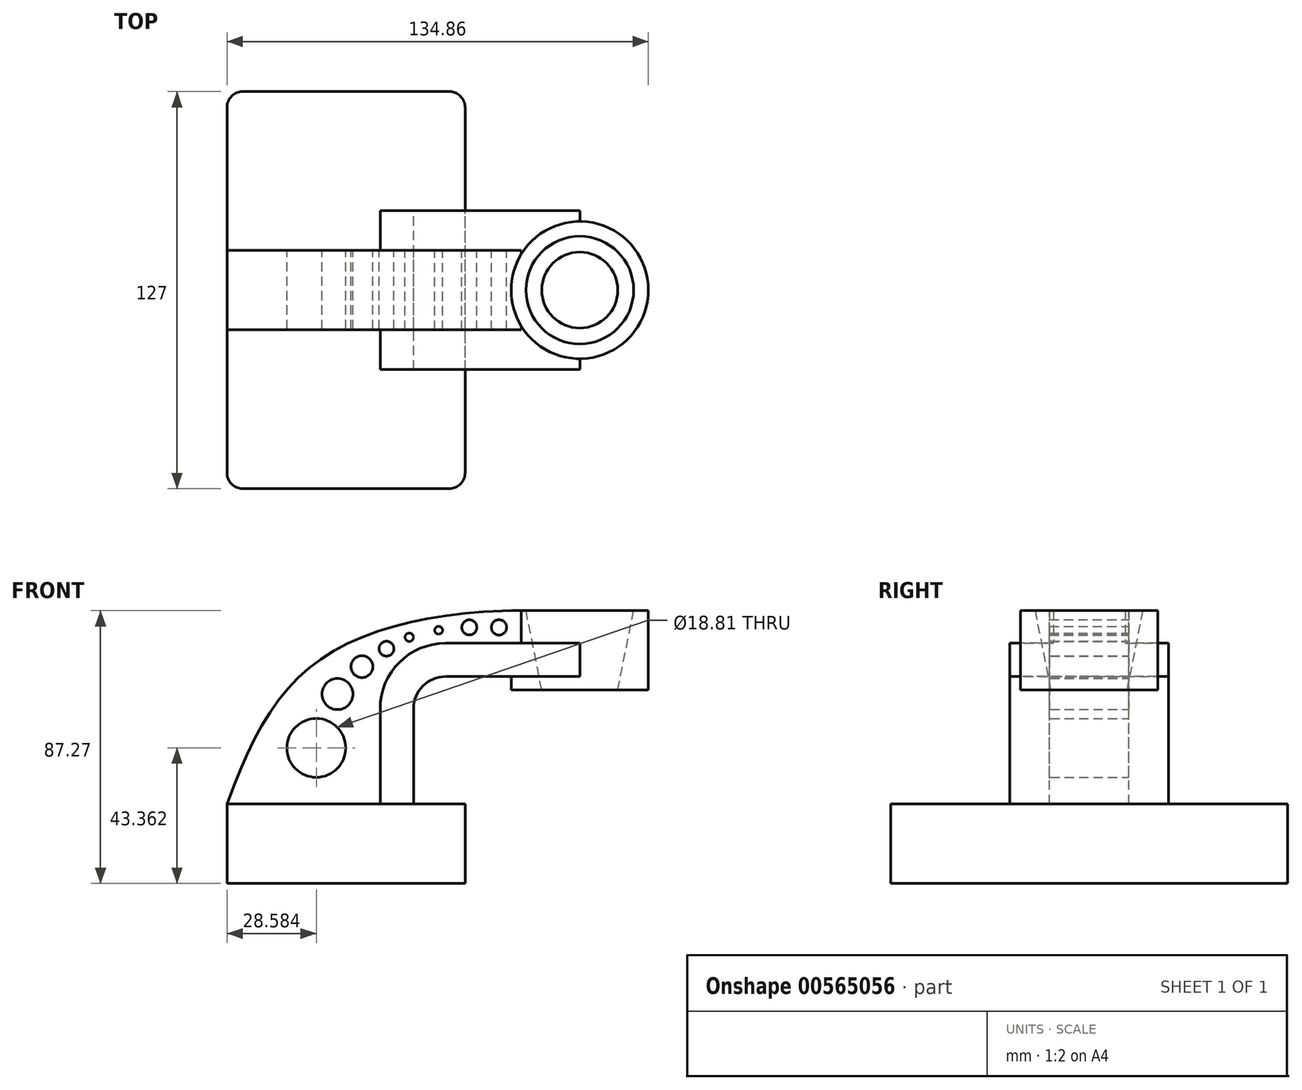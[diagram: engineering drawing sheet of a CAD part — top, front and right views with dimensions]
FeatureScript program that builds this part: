
annotation { "Feature Type Name" : "Feature", "Feature Type Description" : "" }
export const myFeature = defineFeature(function(context is Context, id is Id, definition is map)
    precondition{}
    {
        {
            var Q0;
            Q0=qCreatedBy(makeId("Front.planeOp"),FACE);
            var sketch = newSketch(context, id + "F0", { "sketchPlane" : qUnion([Q0])});
            skLineSegment(sketch, "E0.bottom", {"start": v(38.1, 12.7) * mm, "end": v(-38.1, 12.7) * mm});
            skLineSegment(sketch, "E0.top", {"start": v(38.1, -12.7) * mm, "end": v(-38.1, -12.7) * mm});
            skLineSegment(sketch, "E0.left", {"start": v(38.1, 12.7) * mm, "end": v(38.1, -12.7) * mm});
            skLineSegment(sketch, "E0.right", {"start": v(-38.1, 12.7) * mm, "end": v(-38.1, -12.7) * mm});
            skPoint(sketch, "E0.middle", {"position": v(0, 0) * mm});
            skLineSegment(sketch, "E1.bottom", {"start": v(96.76, 74.57) * mm, "end": v(56.12, 74.57) * mm});
            skLineSegment(sketch, "E1.top", {"start": v(96.76, 49.17) * mm, "end": v(56.12, 49.17) * mm});
            skLineSegment(sketch, "E1.left", {"start": v(96.76, 74.57) * mm, "end": v(96.76, 49.17) * mm});
            skLineSegment(sketch, "E1.right", {"start": v(56.12, 74.57) * mm, "end": v(56.12, 49.17) * mm});
            skPoint(sketch, "E1.middle", {"position": v(76.44, 61.87) * mm});
            skLineSegment(sketch, "E2", {"start": v(21.59, 12.7) * mm, "end": v(21.59, 43.18) * mm});
            skArc(sketch, "E3", {"start": v(31.88, 53.48) * mm, "mid": v(24.6, 50.46) * mm, "end": v(21.59, 43.18) * mm});
            skLineSegment(sketch, "E4", {"start": v(31.88, 53.48) * mm, "end": v(74.8, 53.48) * mm});
            skLineSegment(sketch, "E5.0", {"start": v(31.88, 64.15) * mm, "end": v(74.8, 64.15) * mm});
            skArc(sketch, "E5.1", {"start": v(31.88, 64.15) * mm, "mid": v(17.06, 58) * mm, "end": v(10.92, 43.18) * mm});
            skLineSegment(sketch, "E5.2", {"start": v(10.92, 12.7) * mm, "end": v(10.92, 43.18) * mm});
            skLineSegment(sketch, "E6", {"start": v(74.8, 49.17) * mm, "end": v(74.8, 74.57) * mm});
            skFitSpline(sketch, "E7", {"points": [v(-38.1, 12.7) * mm, v(-8.19, 58.97) * mm, v(56.12, 74.57) * mm], "startDerivative": vector(48.03, 130.43) * mm, "endDerivative": vector(140.44, 0) * mm});
            skLineSegment(sketch, "E8", {"start": v(86.96, 74.57) * mm, "end": v(86.96, 49.17) * mm});
            skLineSegment(sketch, "E9", {"start": v(86.96, 49.17) * mm, "end": v(92.04, 74.57) * mm});
            skLineSegment(sketch, "E10", {"start": v(92.04, 74.57) * mm, "end": v(86.96, 74.57) * mm});
            skCircle(sketch, "E11", {"center": v(-9.52, 30.66) * mm, "radius": 9.4 * mm});
            skCircle(sketch, "E12", {"center": v(-2.74, 47.88) * mm, "radius": 4.96 * mm});
            skCircle(sketch, "E13", {"center": v(5.1, 56.65) * mm, "radius": 3.49 * mm});
            skCircle(sketch, "E14", {"center": v(12.95, 62.4) * mm, "radius": 2.38 * mm});
            skCircle(sketch, "E15", {"center": v(20.24, 66.05) * mm, "radius": 1.35 * mm});
            skCircle(sketch, "E16", {"center": v(29.63, 68.3) * mm, "radius": 1.27 * mm});
            skCircle(sketch, "E17", {"center": v(39.47, 69.2) * mm, "radius": 2.42 * mm});
            skCircle(sketch, "E18", {"center": v(48.96, 69.2) * mm, "radius": 2.45 * mm});
            skSolve(sketch);
        }
        {
            var Q0;
            Q0=makeQuery(id+"F0.imprint","IMPRINT",FACE,{"disambiguationData":[TD([[makeQuery(id+"F0.imprint","IMPRINT",EDGE,{"derivedFrom":sQuery(id+"F0.wireOp",EDGE,"E0.top")}),-1.0]])]});
            extrude(context, id + "F1", {"entities" : qUnion([Q0]), "endBound" : BoundingType.SYMMETRIC, "depth" : 127 * mm, "offsetDistance" : 25.4 * mm});
        }
        {
            var Q0;
            {var subQ1=sQuery(id+"F0.wireOp",EDGE,"E2");Q0=makeQuery(id+"F0.imprint","IMPRINT",FACE,{"disambiguationData":[TD([[makeQuery(id+"F0.imprint","IMPRINT",EDGE,{"derivedFrom":subQ1}),1.0]])]});}
            var Q1;
            {var subQ0=sQuery(id+"F0.wireOp",EDGE,"E4");var subQ1=sQuery(id+"F0.wireOp",EDGE,"E1.right");var subQ2=makeQuery(id+"F0.imprint","INTERSECT",VERTEX,{"derivedFrom":[subQ1,subQ0]});Q1=makeQuery(id+"F0.imprint","IMPRINT",FACE,{"disambiguationData":[TD([[makeQuery(id+"F0.imprint","IMPRINT",EDGE,{"disambiguationData":[TD([[subQ2,1.0]])],"derivedFrom":subQ1}),1.0]])]});}
            extrude(context, id + "F2", {"entities" : qUnion([Q0, Q1]), "operationType" : NewBodyOperationType.ADD, "endBound" : BoundingType.SYMMETRIC, "depth" : 50.8 * mm, "offsetDistance" : 25.4 * mm});
        }
        {
            var Q0;
            {var subQ0=sQuery(id+"F0.wireOp",EDGE,"E5.1");Q0=makeQuery(id+"F0.imprint","IMPRINT",FACE,{"disambiguationData":[TD([[makeQuery(id+"F0.imprint","IMPRINT",EDGE,{"derivedFrom":subQ0}),-1.0]])]});}
            extrude(context, id + "F3", {"entities" : qUnion([Q0]), "operationType" : NewBodyOperationType.ADD, "endBound" : BoundingType.SYMMETRIC, "depth" : 25.4 * mm, "offsetDistance" : 25.4 * mm});
        }
        {
            var Q0;
            {var subQ4=sQuery(id+"F0.wireOp",EDGE,"E1.left");Q0=makeQuery(id+"F0.imprint","IMPRINT",FACE,{"disambiguationData":[TD([[makeQuery(id+"F0.imprint","IMPRINT",EDGE,{"derivedFrom":subQ4}),-1.0]])]});}
            var Q1;
            Q1=sQuery(id+"F0.wireOp",EDGE,"E6");
            revolve(context, id + "F4", {"operationType" : NewBodyOperationType.ADD, "entities" : qUnion([Q0]), "axis" : qUnion([Q1]), "revolveType" : RevolveType.FULL});
        }
        {
            var Q0;
            Q0=makeQuery(id+"F1.opExtrude","CAP_EDGE",EDGE,{"disambiguationData":[OSD([sQuery(id+"F0.wireOp",EDGE,"E0.left")])],"isStart":false});
            var Q1;
            Q1=makeQuery(id+"F1.opExtrude","CAP_EDGE",EDGE,{"disambiguationData":[OSD([sQuery(id+"F0.wireOp",EDGE,"E0.right")])],"isStart":false});
            var Q2;
            Q2=makeQuery(id+"F1.opExtrude","CAP_EDGE",EDGE,{"disambiguationData":[OSD([sQuery(id+"F0.wireOp",EDGE,"E0.left")])],"isStart":true});
            var Q3;
            Q3=makeQuery(id+"F1.opExtrude","CAP_EDGE",EDGE,{"disambiguationData":[OSD([sQuery(id+"F0.wireOp",EDGE,"E0.right")])],"isStart":true});
            fillet(context, id + "F5", {"entities" : qUnion([Q0, Q1, Q2, Q3]), "radius" : 5.08 * mm, "tangentPropagation" : true, "allowEdgeOverflow" : false});
        }
        {
            var Q0;
            {var subQ5=sQuery(id+"F0.wireOp",EDGE,"E8");Q0=makeQuery(id+"F0.imprint","IMPRINT",FACE,{"disambiguationData":[TD([[makeQuery(id+"F0.imprint","IMPRINT",EDGE,{"derivedFrom":subQ5}),-1.0]])]});}
            var Q1;
            Q1=sQuery(id+"F0.wireOp",EDGE,"E6");
            revolve(context, id + "F6", {"operationType" : NewBodyOperationType.REMOVE, "entities" : qUnion([Q0]), "axis" : qUnion([Q1]), "revolveType" : RevolveType.FULL, "oppositeDirection" : true});
        }
        {
            var Q0;
            Q0=makeQuery(id+"F0.imprint","IMPRINT",FACE,{"disambiguationData":[TD([[makeQuery(id+"F0.imprint","IMPRINT",EDGE,{"derivedFrom":sQuery(id+"F0.wireOp",EDGE,"E8")}),1.0]])]});
            var Q1;
            Q1=sQuery(id+"F0.wireOp",EDGE,"E6");
            revolve(context, id + "F7", {"operationType" : NewBodyOperationType.REMOVE, "entities" : qUnion([Q0]), "axis" : qUnion([Q1]), "revolveType" : RevolveType.FULL, "oppositeDirection" : true});
        }
        {
            var Q0;
            Q0=makeQuery(id+"F3.opExtrude","CAP_EDGE",EDGE,{"disambiguationData":[OSD([sQuery(id+"F0.wireOp",EDGE,"E11")])],"isStart":false});
            var Q1;
            Q1=makeQuery(id+"F3.opExtrude","CAP_EDGE",EDGE,{"disambiguationData":[OSD([sQuery(id+"F0.wireOp",EDGE,"E12")])],"isStart":false});
            var Q2;
            Q2=makeQuery(id+"F3.opExtrude","CAP_EDGE",EDGE,{"disambiguationData":[OSD([sQuery(id+"F0.wireOp",EDGE,"E13")])],"isStart":false});
            var Q3;
            Q3=makeQuery(id+"F3.opExtrude","CAP_EDGE",EDGE,{"disambiguationData":[OSD([sQuery(id+"F0.wireOp",EDGE,"E14")])],"isStart":false});
            fillet(context, id + "F8", {"entities" : qUnion([Q0, Q1, Q2, Q3]), "radius" : 0.25 * mm, "tangentPropagation" : true, "allowEdgeOverflow" : false});
        }
    });
